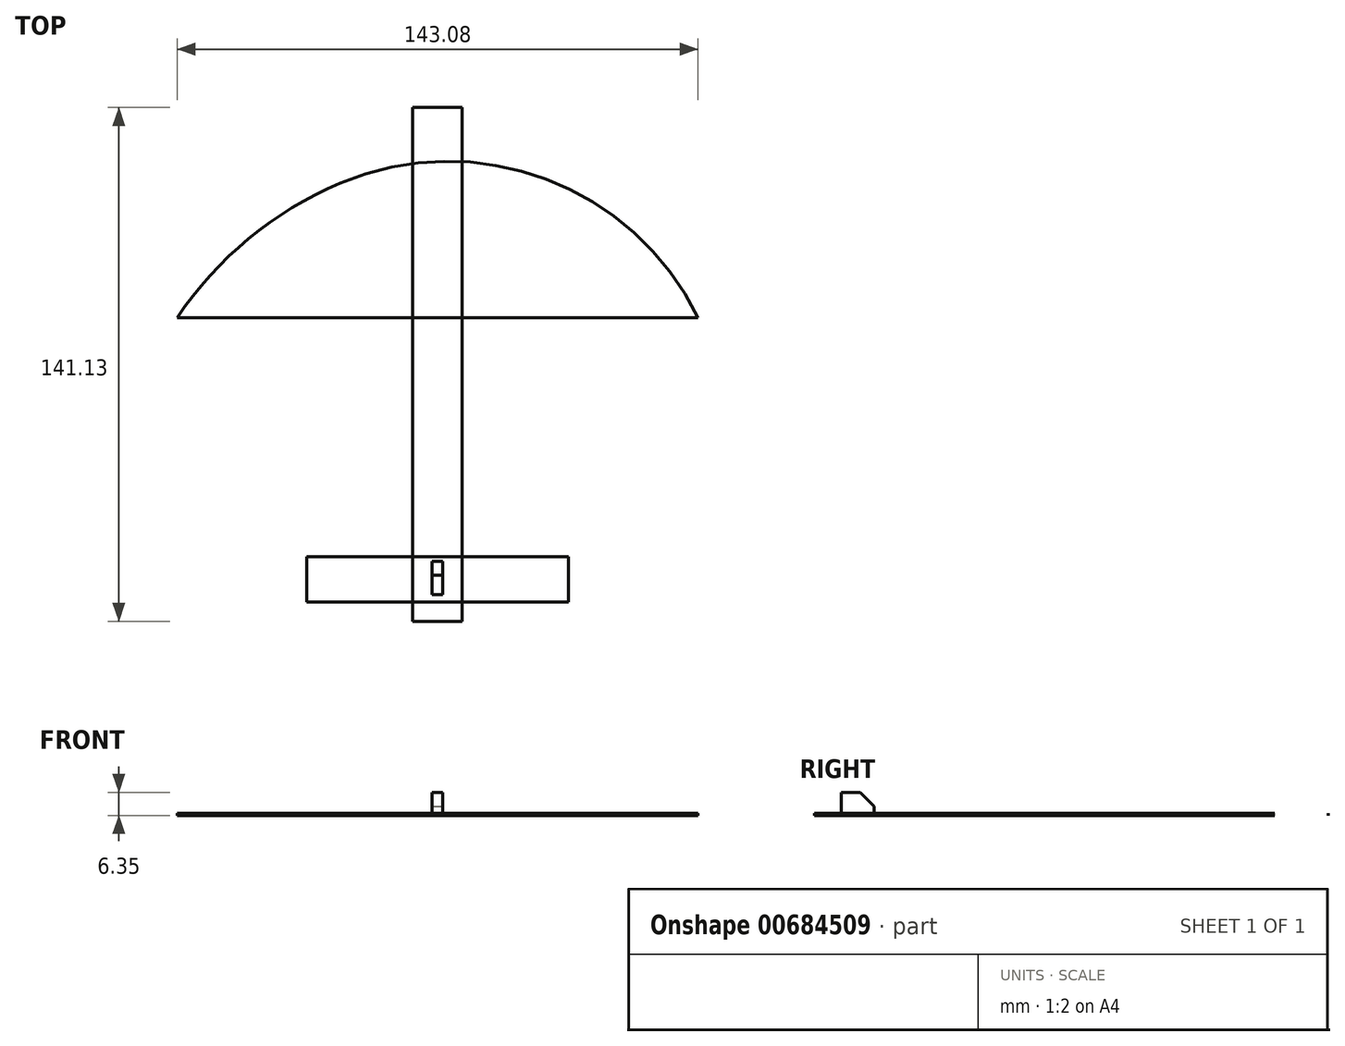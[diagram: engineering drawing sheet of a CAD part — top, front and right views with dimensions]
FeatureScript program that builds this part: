
annotation { "Feature Type Name" : "Feature", "Feature Type Description" : "" }
export const myFeature = defineFeature(function(context is Context, id is Id, definition is map)
    precondition{}
    {
        {
            var Q0;
            Q0=qCreatedBy(makeId("Top.planeOp"),FACE);
            var sketch = newSketch(context, id + "F0", { "sketchPlane" : qUnion([Q0])});
            skLineSegment(sketch, "E0.bottom", {"start": v(71.54, 22.52) * mm, "end": v(-71.54, 22.52) * mm});
            skLineSegment(sketch, "E0.top", {"start": v(71.54, -22.52) * mm, "end": v(-71.54, -22.52) * mm});
            skLineSegment(sketch, "E0.left", {"start": v(71.54, 22.52) * mm, "end": v(71.54, -22.52) * mm});
            skLineSegment(sketch, "E0.right", {"start": v(-71.54, 22.52) * mm, "end": v(-71.54, -22.52) * mm});
            skPoint(sketch, "E0.middle", {"position": v(0, 0) * mm});
            skSolve(sketch);
        }
        {
            var Q0;
            Q0=qCreatedBy(makeId("Top.planeOp"),FACE);
            var sketch = newSketch(context, id + "F1", { "sketchPlane" : qUnion([Q0])});
            skLineSegment(sketch, "E1.bottom", {"start": v(6.78, -105.85) * mm, "end": v(-6.78, -105.85) * mm});
            skLineSegment(sketch, "E1.top", {"start": v(6.78, 35.28) * mm, "end": v(-6.78, 35.28) * mm});
            skLineSegment(sketch, "E1.left", {"start": v(6.78, -105.85) * mm, "end": v(6.78, 35.28) * mm});
            skLineSegment(sketch, "E1.right", {"start": v(-6.78, -105.85) * mm, "end": v(-6.78, 35.28) * mm});
            skPoint(sketch, "E1.middle", {"position": v(0, -35.28) * mm});
            skSolve(sketch);
        }
        {
            var Q0;
            Q0=qCreatedBy(makeId("Top.planeOp"),FACE);
            var sketch = newSketch(context, id + "F2", { "sketchPlane" : qUnion([Q0])});
            skLineSegment(sketch, "E2.bottom", {"start": v(16.9, -100.56) * mm, "end": v(-16.9, -100.56) * mm});
            skLineSegment(sketch, "E2.top", {"start": v(16.9, -88.1) * mm, "end": v(-16.9, -88.1) * mm});
            skLineSegment(sketch, "E2.left", {"start": v(16.9, -100.56) * mm, "end": v(16.9, -88.1) * mm});
            skLineSegment(sketch, "E2.right", {"start": v(-16.9, -100.56) * mm, "end": v(-16.9, -88.1) * mm});
            skPoint(sketch, "E2.middle", {"position": v(0, -94.33) * mm});
            skSolve(sketch);
        }
        {
            var Q0;
            Q0=qCreatedBy(makeId("Top.planeOp"),FACE);
            var sketch = newSketch(context, id + "F3", { "sketchPlane" : qUnion([Q0])});
            skLineSegment(sketch, "E3.bottom", {"start": v(1.45, -98.49) * mm, "end": v(-1.45, -98.49) * mm});
            skLineSegment(sketch, "E3.top", {"start": v(1.45, -89.45) * mm, "end": v(-1.45, -89.45) * mm});
            skLineSegment(sketch, "E3.left", {"start": v(1.45, -98.49) * mm, "end": v(1.45, -89.45) * mm});
            skLineSegment(sketch, "E3.right", {"start": v(-1.45, -98.49) * mm, "end": v(-1.45, -89.45) * mm});
            skPoint(sketch, "E3.middle", {"position": v(0, -93.97) * mm});
            skSolve(sketch);
        }
        {
            var Q0;
            Q0=makeQuery(id+"F0.imprint","IMPRINT",FACE,{"disambiguationData":[TD([[makeQuery(id+"F0.imprint","IMPRINT",EDGE,{"derivedFrom":sQuery(id+"F0.wireOp",EDGE,"E0.bottom")}),1.0]])]});
            extrude(context, id + "F4", {"entities" : qUnion([Q0]), "depth" : 0.64 * mm, "offsetDistance" : 25.4 * mm});
        }
        {
            var Q0;
            Q0=makeQuery(id+"F3.imprint","IMPRINT",FACE,{"disambiguationData":[TD([[makeQuery(id+"F3.imprint","IMPRINT",EDGE,{"derivedFrom":sQuery(id+"F3.wireOp",EDGE,"E3.bottom")}),-1.0]])]});
            extrude(context, id + "F5", {"entities" : qUnion([Q0]), "depth" : 6.35 * mm, "offsetDistance" : 25.4 * mm});
        }
        {
            var Q0;
            Q0=makeQuery(id+"F1.imprint","IMPRINT",FACE,{"disambiguationData":[TD([[makeQuery(id+"F1.imprint","IMPRINT",EDGE,{"derivedFrom":sQuery(id+"F1.wireOp",EDGE,"E1.bottom")}),-1.0]])]});
            var Q1;
            Q1=makeQuery(id+"F2.imprint","IMPRINT",FACE,{"disambiguationData":[TD([[makeQuery(id+"F2.imprint","IMPRINT",EDGE,{"derivedFrom":sQuery(id+"F2.wireOp",EDGE,"E2.bottom")}),-1.0]])]});
            extrude(context, id + "F6", {"entities" : qUnion([Q0, Q1]), "depth" : 0.64 * mm, "offsetDistance" : 25.4 * mm});
        }
        {
            var Q0;
            Q0=makeQuery(id+"F4.opExtrude","SWEPT_EDGE",EDGE,{"disambiguationData":[OSD([sQuery(id+"F0.wireOp",EDGE,"E0.bottom"),sQuery(id+"F0.wireOp",EDGE,"E0.right")])]});
            fillet(context, id + "F7", {"entities" : qUnion([Q0]), "radius" : 101.6 * mm, "tangentPropagation" : true, "allowEdgeOverflow" : false});
        }
        {
            var Q0;
            Q0=makeQuery(id+"F4.opExtrude","SWEPT_EDGE",EDGE,{"disambiguationData":[OSD([sQuery(id+"F0.wireOp",EDGE,"E0.bottom"),sQuery(id+"F0.wireOp",EDGE,"E0.left")])]});
            fillet(context, id + "F8", {"entities" : qUnion([Q0]), "radius" : 76.2 * mm, "tangentPropagation" : true, "allowEdgeOverflow" : false});
        }
        {
            var Q0;
            Q0=makeQuery(id+"F5.opExtrude","CAP_EDGE",EDGE,{"disambiguationData":[OSD([sQuery(id+"F3.wireOp",EDGE,"E3.top")])],"isStart":false});
            chamfer(context, id + "F9", {"entities" : qUnion([Q0]), "width" : 3.8 * mm, "tangentPropagation" : true});
        }
        {
            var Q0;
            Q0=makeQuery(id+"F6.opExtrude","SWEPT_FACE",FACE,{"disambiguationData":[OSD([sQuery(id+"F2.wireOp",EDGE,"E2.right")])]});
            extrude(context, id + "F10", {"entities" : qUnion([Q0]), "operationType" : NewBodyOperationType.ADD, "depth" : 19.05 * mm, "offsetDistance" : 25.4 * mm});
        }
        {
            var Q0;
            Q0=makeQuery(id+"F6.opExtrude","SWEPT_FACE",FACE,{"disambiguationData":[OSD([sQuery(id+"F2.wireOp",EDGE,"E2.left")])]});
            extrude(context, id + "F11", {"entities" : qUnion([Q0]), "operationType" : NewBodyOperationType.ADD, "depth" : 19.05 * mm, "offsetDistance" : 25.4 * mm});
        }
    });
